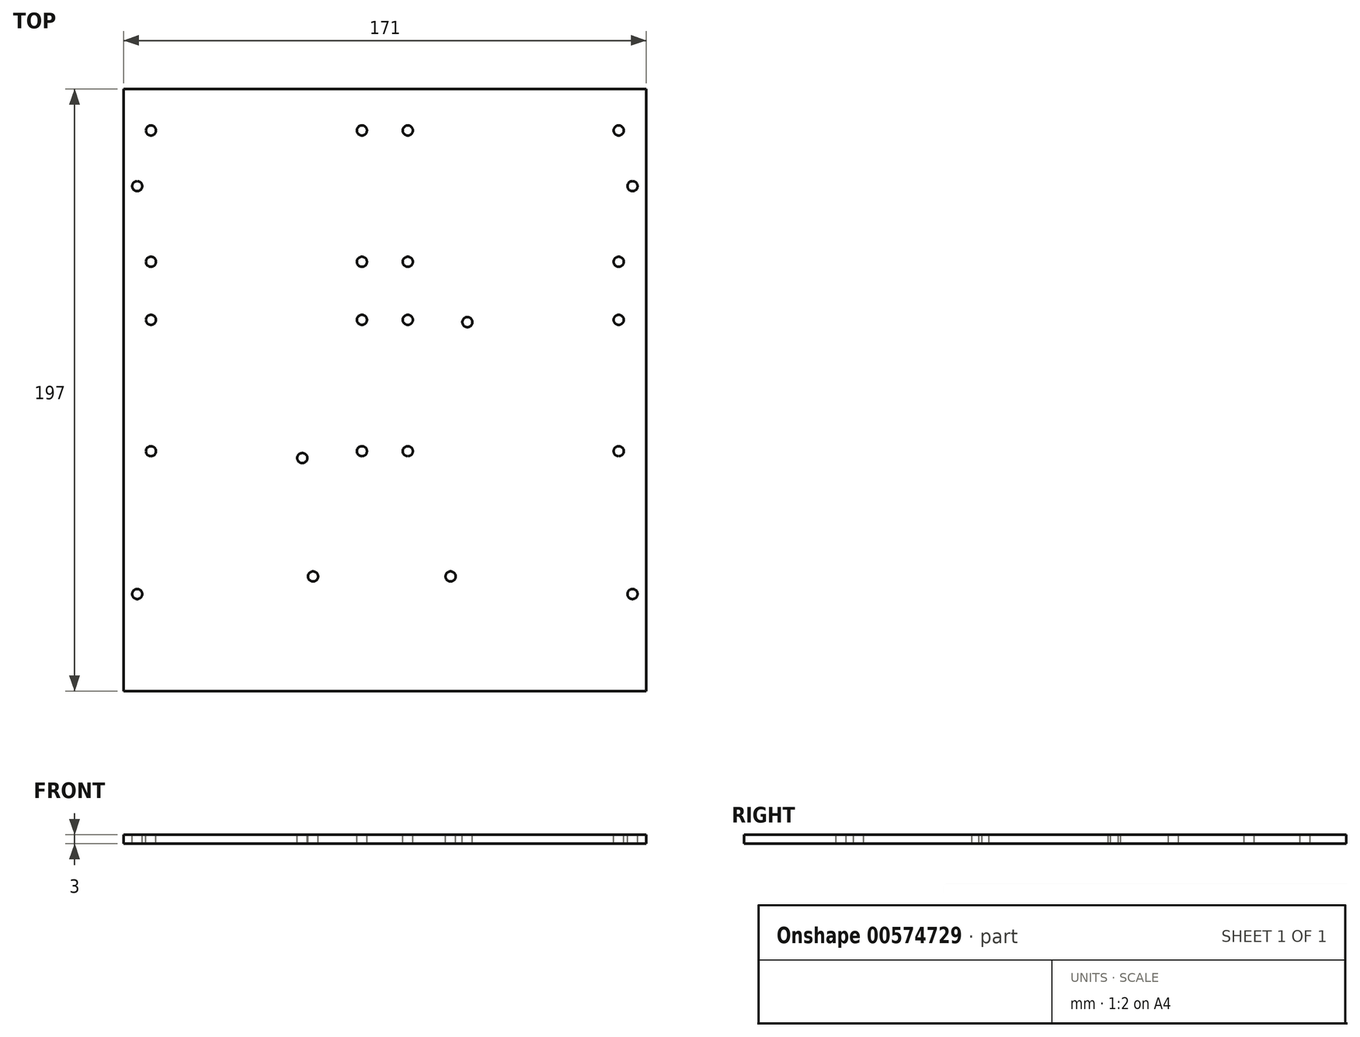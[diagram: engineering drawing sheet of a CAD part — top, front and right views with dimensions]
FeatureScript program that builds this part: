
annotation { "Feature Type Name" : "Feature", "Feature Type Description" : "" }
export const myFeature = defineFeature(function(context is Context, id is Id, definition is map)
    precondition{}
    {
        {
            var Q0;
            Q0=qCreatedBy(makeId("Top.planeOp"),FACE);
            var sketch = newSketch(context, id + "F0", { "sketchPlane" : qUnion([Q0])});
            skLineSegment(sketch, "E0.bottom", {"start": v(-85.5, 98.5) * mm, "end": v(85.5, 98.5) * mm});
            skLineSegment(sketch, "E0.top", {"start": v(-85.5, -98.5) * mm, "end": v(85.5, -98.5) * mm});
            skLineSegment(sketch, "E0.left", {"start": v(-85.5, 98.5) * mm, "end": v(-85.5, -98.5) * mm});
            skLineSegment(sketch, "E0.right", {"start": v(85.5, 98.5) * mm, "end": v(85.5, -98.5) * mm});
            skLineSegment(sketch, "E1", {"start": v(-85.5, 0) * mm, "end": v(85.5, 0) * mm, "construction": true});
            skLineSegment(sketch, "E2", {"start": v(0, -98.5) * mm, "end": v(0, 98.5) * mm, "construction": true});
            skSolve(sketch);
        }
        {
            var Q0;
            Q0=makeQuery(id+"F0.imprint","IMPRINT",FACE,{"disambiguationData":[TD([[makeQuery(id+"F0.imprint","IMPRINT",EDGE,{"derivedFrom":sQuery(id+"F0.wireOp",EDGE,"E0.bottom")}),-1.0]])]});
            extrude(context, id + "F1", {"entities" : qUnion([Q0]), "depth" : 3 * mm, "offsetDistance" : 25 * mm});
        }
        {
            var Q0;
            Q0=makeQuery(id+"F1.opExtrude","CAP_FACE",FACE,{"disambiguationData":[OSD([sQuery(id+"F0.wireOp",EDGE,"E0.bottom"),sQuery(id+"F0.wireOp",EDGE,"E0.top"),sQuery(id+"F0.wireOp",EDGE,"E0.left"),sQuery(id+"F0.wireOp",EDGE,"E0.right")])],"isStart":false});
            var sketch = newSketch(context, id + "F2", { "sketchPlane" : qUnion([Q0])});
            skLineSegment(sketch, "E3.bottom", {"start": v(-79.5, 88.5) * mm, "end": v(-4.5, 88.5) * mm, "construction": true});
            skLineSegment(sketch, "E3.top", {"start": v(-79.5, 38.5) * mm, "end": v(-4.5, 38.5) * mm, "construction": true});
            skLineSegment(sketch, "E3.left", {"start": v(-79.5, 88.5) * mm, "end": v(-79.5, 38.5) * mm, "construction": true});
            skLineSegment(sketch, "E3.right", {"start": v(-4.5, 88.5) * mm, "end": v(-4.5, 38.5) * mm, "construction": true});
            skPoint(sketch, "E4", {"position": v(-76.5, 85) * mm});
            skPoint(sketch, "E5", {"position": v(-7.5, 85) * mm});
            skPoint(sketch, "E6", {"position": v(-7.5, 42) * mm});
            skPoint(sketch, "E7", {"position": v(-76.5, 42) * mm});
            skLineSegment(sketch, "E8", {"start": v(-76.5, 42) * mm, "end": v(-76.5, 85) * mm});
            skLineSegment(sketch, "E9", {"start": v(-7.5, 42) * mm, "end": v(-7.5, 85) * mm});
            skLineSegment(sketch, "E10", {"start": v(-76.5, 85) * mm, "end": v(-79.5, 85) * mm, "construction": true});
            skLineSegment(sketch, "E11", {"start": v(-7.5, 85) * mm, "end": v(-4.5, 85) * mm, "construction": true});
            skLineSegment(sketch, "E12", {"start": v(-76.5, 85) * mm, "end": v(-76.5, 88.5) * mm, "construction": true});
            skLineSegment(sketch, "E13", {"start": v(-76.5, 42) * mm, "end": v(-76.5, 38.5) * mm, "construction": true});
            skLineSegment(sketch, "E14.bottom", {"start": v(4.5, 88.5) * mm, "end": v(79.5, 88.5) * mm, "construction": true});
            skLineSegment(sketch, "E14.top", {"start": v(4.5, 38.5) * mm, "end": v(79.5, 38.5) * mm, "construction": true});
            skLineSegment(sketch, "E14.left", {"start": v(4.5, 88.5) * mm, "end": v(4.5, 38.5) * mm, "construction": true});
            skLineSegment(sketch, "E14.right", {"start": v(79.5, 88.5) * mm, "end": v(79.5, 38.5) * mm, "construction": true});
            skPoint(sketch, "E15", {"position": v(7.5, 85) * mm});
            skPoint(sketch, "E16", {"position": v(76.5, 85) * mm});
            skPoint(sketch, "E17", {"position": v(76.5, 42) * mm});
            skPoint(sketch, "E18", {"position": v(7.5, 42) * mm});
            skLineSegment(sketch, "E19", {"start": v(7.5, 42) * mm, "end": v(7.5, 85) * mm});
            skLineSegment(sketch, "E20", {"start": v(76.5, 42) * mm, "end": v(76.5, 85) * mm});
            skLineSegment(sketch, "E21", {"start": v(7.5, 85) * mm, "end": v(4.5, 85) * mm, "construction": true});
            skLineSegment(sketch, "E22", {"start": v(76.5, 85) * mm, "end": v(79.5, 85) * mm, "construction": true});
            skLineSegment(sketch, "E23", {"start": v(7.5, 85) * mm, "end": v(7.5, 88.5) * mm, "construction": true});
            skLineSegment(sketch, "E24", {"start": v(7.5, 42) * mm, "end": v(7.5, 38.5) * mm, "construction": true});
            skLineSegment(sketch, "E25.bottom", {"start": v(-79.5, 26.5) * mm, "end": v(-4.5, 26.5) * mm, "construction": true});
            skLineSegment(sketch, "E25.top", {"start": v(-79.5, -23.5) * mm, "end": v(-4.5, -23.5) * mm, "construction": true});
            skLineSegment(sketch, "E25.left", {"start": v(-79.5, 26.5) * mm, "end": v(-79.5, -23.5) * mm, "construction": true});
            skLineSegment(sketch, "E25.right", {"start": v(-4.5, 26.5) * mm, "end": v(-4.5, -23.5) * mm, "construction": true});
            skPoint(sketch, "E26", {"position": v(-76.5, 23) * mm});
            skPoint(sketch, "E27", {"position": v(-7.5, 23) * mm});
            skPoint(sketch, "E28", {"position": v(-7.5, -20) * mm});
            skPoint(sketch, "E29", {"position": v(-76.5, -20) * mm});
            skLineSegment(sketch, "E30", {"start": v(-76.5, -20) * mm, "end": v(-76.5, 23) * mm});
            skLineSegment(sketch, "E31", {"start": v(-7.5, -20) * mm, "end": v(-7.5, 23) * mm});
            skLineSegment(sketch, "E32", {"start": v(-76.5, 23) * mm, "end": v(-79.5, 23) * mm, "construction": true});
            skLineSegment(sketch, "E33", {"start": v(-7.5, 23) * mm, "end": v(-4.5, 23) * mm, "construction": true});
            skLineSegment(sketch, "E34", {"start": v(-76.5, 23) * mm, "end": v(-76.5, 26.5) * mm, "construction": true});
            skLineSegment(sketch, "E35", {"start": v(-76.5, -20) * mm, "end": v(-76.5, -23.5) * mm, "construction": true});
            skLineSegment(sketch, "E36.bottom", {"start": v(4.5, 26.5) * mm, "end": v(79.5, 26.5) * mm, "construction": true});
            skLineSegment(sketch, "E36.top", {"start": v(4.5, -23.5) * mm, "end": v(79.5, -23.5) * mm, "construction": true});
            skLineSegment(sketch, "E36.left", {"start": v(4.5, 26.5) * mm, "end": v(4.5, -23.5) * mm, "construction": true});
            skLineSegment(sketch, "E36.right", {"start": v(79.5, 26.5) * mm, "end": v(79.5, -23.5) * mm, "construction": true});
            skPoint(sketch, "E37", {"position": v(7.5, 23) * mm});
            skPoint(sketch, "E38", {"position": v(76.5, 23) * mm});
            skPoint(sketch, "E39", {"position": v(76.5, -20) * mm});
            skPoint(sketch, "E40", {"position": v(7.5, -20) * mm});
            skLineSegment(sketch, "E41", {"start": v(7.5, -20) * mm, "end": v(7.5, 23) * mm});
            skLineSegment(sketch, "E42", {"start": v(76.5, -20) * mm, "end": v(76.5, 23) * mm});
            skLineSegment(sketch, "E43", {"start": v(7.5, 23) * mm, "end": v(4.5, 23) * mm, "construction": true});
            skLineSegment(sketch, "E44", {"start": v(76.5, 23) * mm, "end": v(79.5, 23) * mm, "construction": true});
            skLineSegment(sketch, "E45", {"start": v(7.5, 23) * mm, "end": v(7.5, 26.5) * mm, "construction": true});
            skLineSegment(sketch, "E46", {"start": v(7.5, -20) * mm, "end": v(7.5, -23.5) * mm, "construction": true});
            skLineSegment(sketch, "E47.bottom", {"start": v(-26, -38.5) * mm, "end": v(24, -38.5) * mm, "construction": true});
            skLineSegment(sketch, "E47.top", {"start": v(-26, -83.5) * mm, "end": v(24, -83.5) * mm, "construction": true});
            skLineSegment(sketch, "E47.left", {"start": v(-26, -38.5) * mm, "end": v(-26, -83.5) * mm, "construction": true});
            skLineSegment(sketch, "E47.right", {"start": v(24, -38.5) * mm, "end": v(24, -83.5) * mm, "construction": true});
            skPoint(sketch, "E48", {"position": v(-23.5, -61) * mm});
            skPoint(sketch, "E49", {"position": v(21.5, -61) * mm});
            skLineSegment(sketch, "E50", {"start": v(-26, -61) * mm, "end": v(-23.5, -61) * mm});
            skLineSegment(sketch, "E51", {"start": v(21.5, -61) * mm, "end": v(24, -61) * mm});
            skSolve(sketch);
        }
        {
            var Q0;
            Q0=sQuery(id+"F2.wireOp",VERTEX,"E4");
            var Q1;
            Q1=sQuery(id+"F2.wireOp",VERTEX,"E5");
            var Q2;
            Q2=sQuery(id+"F2.wireOp",VERTEX,"E6");
            var Q3;
            Q3=sQuery(id+"F2.wireOp",VERTEX,"E7");
            var Q4;
            Q4=sQuery(id+"F2.wireOp",VERTEX,"E29");
            var Q5;
            Q5=sQuery(id+"F2.wireOp",VERTEX,"E26");
            var Q6;
            Q6=sQuery(id+"F2.wireOp",VERTEX,"E27");
            var Q7;
            Q7=sQuery(id+"F2.wireOp",VERTEX,"E28");
            var Q8;
            Q8=sQuery(id+"F2.wireOp",VERTEX,"E40");
            var Q9;
            Q9=sQuery(id+"F2.wireOp",VERTEX,"E37");
            var Q10;
            Q10=sQuery(id+"F2.wireOp",VERTEX,"E38");
            var Q11;
            Q11=sQuery(id+"F2.wireOp",VERTEX,"E39");
            var Q12;
            Q12=sQuery(id+"F2.wireOp",VERTEX,"E18");
            var Q13;
            Q13=sQuery(id+"F2.wireOp",VERTEX,"E17");
            var Q14;
            Q14=sQuery(id+"F2.wireOp",VERTEX,"E16");
            var Q15;
            Q15=sQuery(id+"F2.wireOp",VERTEX,"E15");
            var Q16;
            Q16=sQuery(id+"F2.wireOp",VERTEX,"E49");
            var Q17;
            Q17=sQuery(id+"F2.wireOp",VERTEX,"E48");
            var Q18;
            Q18=makeQuery(id+"F1.opExtrude","SWEPT_BODY",BODY,{"disambiguationData":[OSD([sQuery(id+"F0.wireOp",EDGE,"E0.bottom"),sQuery(id+"F0.wireOp",EDGE,"E0.top"),sQuery(id+"F0.wireOp",EDGE,"E0.left"),sQuery(id+"F0.wireOp",EDGE,"E0.right")])]});
            hole(context, id + "F3", {"style" : HoleStyle.SIMPLE, "endStyle" : HoleEndStyle.THROUGH, "standardTappedOrClearance" : lookupTablePath({ "standard" : "ISO", "fit" : "Normal", "size" : "M3", "type" : "Clearance" }), "standardBlindInLast" : lookupTablePath({ "fit" : "Standard", "standard" : "ISO", "size" : "M3", "type" : "Clearance" }), "holeDiameter" : 3.3 * mm, "majorDiameter" : 5 * mm, "isTappedThrough" : true, "tappedDepth" : 15 * mm, "tapClearance" : 0, "startFromSketch" : true, "locations" : qUnion([Q0, Q1, Q2, Q3, Q4, Q5, Q6, Q7, Q8, Q9, Q10, Q11, Q12, Q13, Q14, Q15, Q16, Q17]), "scope" : qUnion([Q18])});
        }
        {
            var Q0;
            Q0=makeQuery(id+"F1.opExtrude","CAP_FACE",FACE,{"disambiguationData":[OSD([sQuery(id+"F0.wireOp",EDGE,"E0.bottom"),sQuery(id+"F0.wireOp",EDGE,"E0.top"),sQuery(id+"F0.wireOp",EDGE,"E0.left"),sQuery(id+"F0.wireOp",EDGE,"E0.right")])],"isStart":false});
            var sketch = newSketch(context, id + "F4", { "sketchPlane" : qUnion([Q0])});
            skLineSegment(sketch, "E52.bottom", {"start": v(-81, 66.75) * mm, "end": v(81, 66.75) * mm});
            skLineSegment(sketch, "E52.top", {"start": v(-81, -66.75) * mm, "end": v(81, -66.75) * mm});
            skLineSegment(sketch, "E52.left", {"start": v(-81, 66.75) * mm, "end": v(-81, -66.75) * mm});
            skLineSegment(sketch, "E52.right", {"start": v(81, 66.75) * mm, "end": v(81, -66.75) * mm});
            skLineSegment(sketch, "E53", {"start": v(-81, 22.25) * mm, "end": v(81, 22.25) * mm});
            skLineSegment(sketch, "E54", {"start": v(-81, -22.25) * mm, "end": v(81, -22.25) * mm});
            skLineSegment(sketch, "E55", {"start": v(-27, 66.75) * mm, "end": v(-27, -66.75) * mm});
            skLineSegment(sketch, "E56", {"start": v(27, 66.75) * mm, "end": v(27, -66.75) * mm});
            skPoint(sketch, "E57", {"position": v(-81, 66.75) * mm});
            skPoint(sketch, "E58", {"position": v(81, 66.75) * mm});
            skPoint(sketch, "E59", {"position": v(81, -66.75) * mm});
            skPoint(sketch, "E60", {"position": v(-81, -66.75) * mm});
            skPoint(sketch, "E61", {"position": v(-27, -22.25) * mm});
            skPoint(sketch, "E62", {"position": v(27, 22.25) * mm});
            skLineSegment(sketch, "E63", {"start": v(-17.24, -66.75) * mm, "end": v(-17.24, -98.5) * mm, "construction": true});
            skLineSegment(sketch, "E64", {"start": v(-22.47, 66.75) * mm, "end": v(-22.47, 98.5) * mm, "construction": true});
            skSolve(sketch);
        }
        {
            var Q0;
            Q0=sQuery(id+"F4.wireOp",VERTEX,"E57");
            var Q1;
            Q1=sQuery(id+"F4.wireOp",VERTEX,"E58");
            var Q2;
            Q2=sQuery(id+"F4.wireOp",VERTEX,"E62");
            var Q3;
            Q3=sQuery(id+"F4.wireOp",VERTEX,"E61");
            var Q4;
            Q4=sQuery(id+"F4.wireOp",VERTEX,"E60");
            var Q5;
            Q5=sQuery(id+"F4.wireOp",VERTEX,"E59");
            var Q6;
            Q6=makeQuery(id+"F1.opExtrude","SWEPT_BODY",BODY,{"disambiguationData":[OSD([sQuery(id+"F0.wireOp",EDGE,"E0.bottom"),sQuery(id+"F0.wireOp",EDGE,"E0.top"),sQuery(id+"F0.wireOp",EDGE,"E0.left"),sQuery(id+"F0.wireOp",EDGE,"E0.right")])]});
            hole(context, id + "F5", {"style" : HoleStyle.SIMPLE, "endStyle" : HoleEndStyle.THROUGH, "standardTappedOrClearance" : lookupTablePath({ "standard" : "ISO", "fit" : "Normal", "size" : "M3", "type" : "Clearance" }), "standardBlindInLast" : lookupTablePath({ "fit" : "Standard", "standard" : "ISO", "size" : "M3", "type" : "Clearance" }), "holeDiameter" : 3.3 * mm, "majorDiameter" : 5 * mm, "isTappedThrough" : true, "tappedDepth" : 15 * mm, "tapClearance" : 3, "startFromSketch" : true, "locations" : qUnion([Q0, Q1, Q2, Q3, Q4, Q5]), "scope" : qUnion([Q6])});
        }
    });
